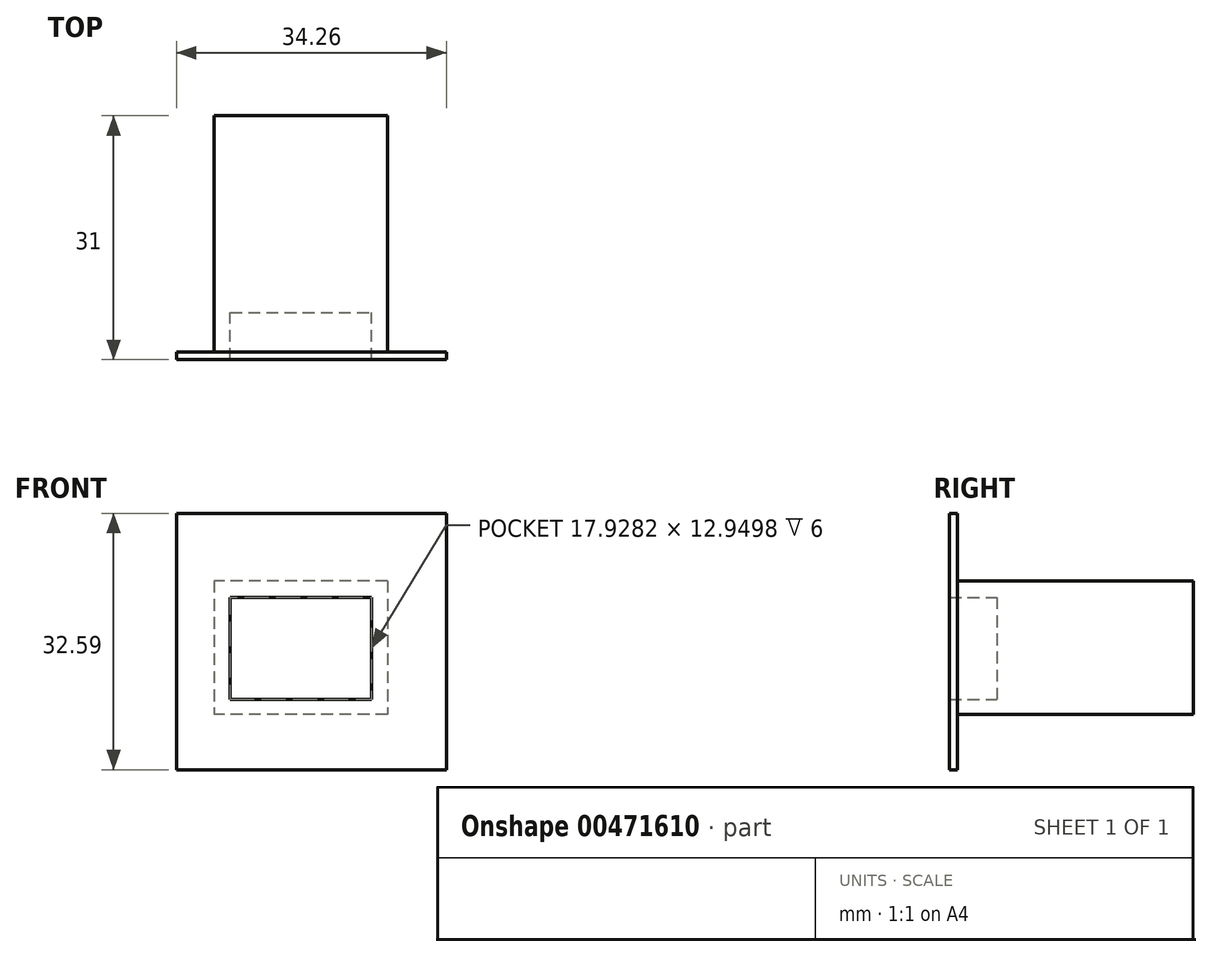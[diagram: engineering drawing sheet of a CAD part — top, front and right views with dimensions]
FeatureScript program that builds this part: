
annotation { "Feature Type Name" : "Feature", "Feature Type Description" : "" }
export const myFeature = defineFeature(function(context is Context, id is Id, definition is map)
    precondition{}
    {
        {
            var Q0;
            Q0=qCreatedBy(makeId("Front.planeOp"),FACE);
            var sketch = newSketch(context, id + "F0", { "sketchPlane" : qUnion([Q0])});
            skLineSegment(sketch, "E0.bottom", {"start": v(11, 8.5) * mm, "end": v(-11, 8.5) * mm});
            skLineSegment(sketch, "E0.top", {"start": v(11, -8.5) * mm, "end": v(-11, -8.5) * mm});
            skLineSegment(sketch, "E0.left", {"start": v(11, 8.5) * mm, "end": v(11, -8.5) * mm});
            skLineSegment(sketch, "E0.right", {"start": v(-11, 8.5) * mm, "end": v(-11, -8.5) * mm});
            skPoint(sketch, "E0.middle", {"position": v(0, 0) * mm});
            skLineSegment(sketch, "E1", {"start": v(0, -8.5) * mm, "end": v(-3.5, -8.5) * mm});
            skLineSegment(sketch, "E2", {"start": v(-3.5, -8.5) * mm, "end": v(-3.5, -1.5) * mm});
            skLineSegment(sketch, "E3", {"start": v(-3.5, -1.5) * mm, "end": v(3.5, -1.5) * mm});
            skLineSegment(sketch, "E4", {"start": v(3.5, -1.5) * mm, "end": v(3.5, -8.5) * mm});
            skLineSegment(sketch, "E5", {"start": v(3.5, -8.5) * mm, "end": v(-3.5, -8.5) * mm});
            skSolve(sketch);
        }
        {
            var Q0;
            Q0=makeQuery(id+"F0.imprint","IMPRINT",FACE,{"disambiguationData":[TD([[makeQuery(id+"F0.imprint","IMPRINT",EDGE,{"derivedFrom":sQuery(id+"F0.wireOp",EDGE,"E0.bottom")}),1.0]])]});
            var Q1;
            {var subQ0=sQuery(id+"F0.wireOp",EDGE,"E2");Q1=makeQuery(id+"F0.imprint","IMPRINT",FACE,{"disambiguationData":[TD([[makeQuery(id+"F0.imprint","IMPRINT",EDGE,{"derivedFrom":subQ0}),-1.0]])]});}
            extrude(context, id + "F1", {"entities" : qUnion([Q0, Q1]), "depth" : 25 * mm});
        }
        {
            var Q1;
            Q1=makeQuery(id+"F1.opExtrude","CAP_FACE",FACE,{"disambiguationData":[OSD([sQuery(id+"F0.wireOp",EDGE,"E0.bottom"),sQuery(id+"F0.wireOp",EDGE,"E0.top"),sQuery(id+"F0.wireOp",EDGE,"E0.left"),sQuery(id+"F0.wireOp",EDGE,"E0.right"),sQuery(id+"F0.wireOp",EDGE,"E5")])],"isStart":false});
            var Q2;
            {var subQ0=sQuery(id+"F0.wireOp",EDGE,"E2");Q2=makeQuery(id+"F0.imprint","IMPRINT",FACE,{"disambiguationData":[TD([[makeQuery(id+"F0.imprint","IMPRINT",EDGE,{"derivedFrom":subQ0}),-1.0]])]});}
            loft(context, id + "F2", {"sheetProfilesArray" : [{ "sheetProfileEntities" : qUnion([Q1]) }, { "sheetProfileEntities" : qUnion([Q2]) }]});
        }
        {
            var Q0;
            {var subQ0=sQuery(id+"F0.wireOp",EDGE,"E2");Q0=makeQuery(id+"F2.opLoft","CAP_FACE",FACE,{"disambiguationData":[OSD([makeQuery(id+"F0.imprint","IMPRINT",FACE,{"disambiguationData":[TD([[makeQuery(id+"F0.imprint","IMPRINT",EDGE,{"derivedFrom":subQ0}),-1.0]])]})])],"isStart":true});}
            var Q1;
            Q1=makeQuery(id+"F2.opLoft","CAP_FACE",FACE,{"disambiguationData":[OSD([sQuery(id+"F0.wireOp",EDGE,"E0.bottom"),sQuery(id+"F0.wireOp",EDGE,"E0.top"),sQuery(id+"F0.wireOp",EDGE,"E0.left"),sQuery(id+"F0.wireOp",EDGE,"E0.right"),sQuery(id+"F0.wireOp",EDGE,"E5")])],"isStart":true});
            shell(context, id + "F3", {"entities" : qUnion([Q0, Q1]), "thickness" : 1.95 * mm});
        }
        {
            var Q0;
            Q0=makeQuery(id+"F2.opLoft","CAP_FACE",FACE,{"disambiguationData":[OSD([sQuery(id+"F0.wireOp",EDGE,"E0.bottom"),sQuery(id+"F0.wireOp",EDGE,"E0.top"),sQuery(id+"F0.wireOp",EDGE,"E0.left"),sQuery(id+"F0.wireOp",EDGE,"E0.right"),sQuery(id+"F0.wireOp",EDGE,"E5")])],"isStart":true});
            extrude(context, id + "F4", {"entities" : qUnion([Q0]), "operationType" : NewBodyOperationType.ADD, "depth" : 5 * mm});
        }
        {
            var Q0;
            Q0=makeQuery(id+"F4.opExtrude","CAP_FACE",FACE,{"disambiguationData":[OSD([sQuery(id+"F0.wireOp",EDGE,"E0.bottom"),sQuery(id+"F0.wireOp",EDGE,"E0.top"),sQuery(id+"F0.wireOp",EDGE,"E0.left"),sQuery(id+"F0.wireOp",EDGE,"E0.right"),sQuery(id+"F0.wireOp",EDGE,"E5")])],"isStart":false});
            var sketch = newSketch(context, id + "F5", { "sketchPlane" : qUnion([Q0])});
            skLineSegment(sketch, "E6.0.0", {"start": v(-11, -8.5) * mm, "end": v(-11, 8.5) * mm});
            skLineSegment(sketch, "E6.0.1", {"start": v(-11, -8.5) * mm, "end": v(11, -8.5) * mm});
            skLineSegment(sketch, "E6.0.2", {"start": v(11, -8.5) * mm, "end": v(11, 8.5) * mm});
            skLineSegment(sketch, "E6.0.3", {"start": v(-11, 8.5) * mm, "end": v(11, 8.5) * mm});
            skLineSegment(sketch, "E7.bottom", {"start": v(-15.78, -15.5) * mm, "end": v(18.48, -15.5) * mm});
            skLineSegment(sketch, "E7.top", {"start": v(-15.78, 17.08) * mm, "end": v(18.48, 17.08) * mm});
            skLineSegment(sketch, "E7.left", {"start": v(-15.78, -15.5) * mm, "end": v(-15.78, 17.08) * mm});
            skLineSegment(sketch, "E7.right", {"start": v(18.48, -15.5) * mm, "end": v(18.48, 17.08) * mm});
            skSolve(sketch);
        }
        {
            var Q0;
            Q0=makeQuery(id+"F5.imprint","IMPRINT",FACE,{"disambiguationData":[TD([[makeQuery(id+"F5.imprint","IMPRINT",EDGE,{"derivedFrom":sQuery(id+"F5.wireOp",EDGE,"E6.0.0")}),1.0]])]});
            var Q1;
            Q1=makeQuery(id+"F5.imprint","IMPRINT",FACE,{"disambiguationData":[TD([[makeQuery(id+"F5.imprint","IMPRINT",EDGE,{"derivedFrom":sQuery(id+"F5.wireOp",EDGE,"E6.0.0")}),-1.0]])]});
            extrude(context, id + "F6", {"entities" : qUnion([Q0, Q1]), "operationType" : NewBodyOperationType.ADD, "depth" : 1 * mm});
        }
    });
